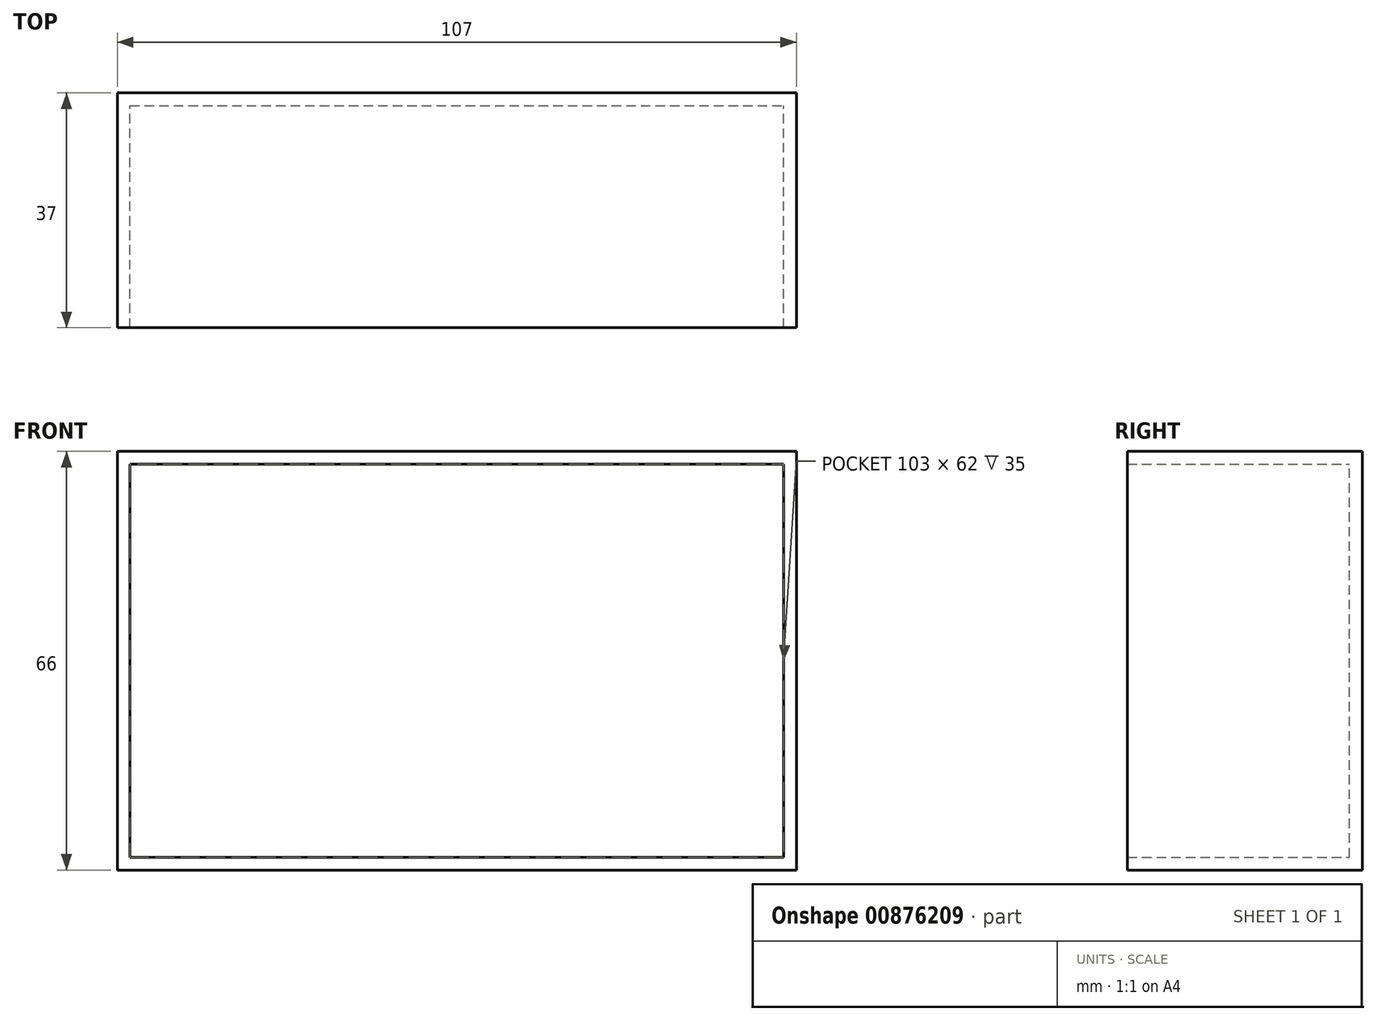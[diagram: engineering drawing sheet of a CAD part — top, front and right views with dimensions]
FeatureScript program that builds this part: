
annotation { "Feature Type Name" : "Feature", "Feature Type Description" : "" }
export const myFeature = defineFeature(function(context is Context, id is Id, definition is map)
    precondition{}
    {
        {
            var Q0;
            Q0=qCreatedBy(makeId("Front.planeOp"),FACE);
            var sketch = newSketch(context, id + "F0", { "sketchPlane" : qUnion([Q0])});
            skLineSegment(sketch, "E0.bottom", {"start": v(0, 0) * mm, "end": v(107, 0) * mm});
            skLineSegment(sketch, "E0.top", {"start": v(0, 66) * mm, "end": v(107, 66) * mm});
            skLineSegment(sketch, "E0.left", {"start": v(0, 0) * mm, "end": v(0, 66) * mm});
            skLineSegment(sketch, "E0.right", {"start": v(107, 0) * mm, "end": v(107, 66) * mm});
            skSolve(sketch);
        }
        {
            var Q0;
            Q0=qSketchRegion(id+"F0",true);
            extrude(context, id + "F1", {"entities" : qUnion([Q0]), "depth" : 37 * mm, "offsetDistance" : 25 * mm});
        }
        {
            var Q0;
            Q0=makeQuery(id+"F1.opExtrude","CAP_FACE",FACE,{"disambiguationData":[OSD([sQuery(id+"F0.wireOp",EDGE,"E0.bottom"),sQuery(id+"F0.wireOp",EDGE,"E0.top"),sQuery(id+"F0.wireOp",EDGE,"E0.left"),sQuery(id+"F0.wireOp",EDGE,"E0.right")])],"isStart":false});
            shell(context, id + "F2", {"entities" : qUnion([Q0]), "thickness" : 2 * mm});
        }
    });
